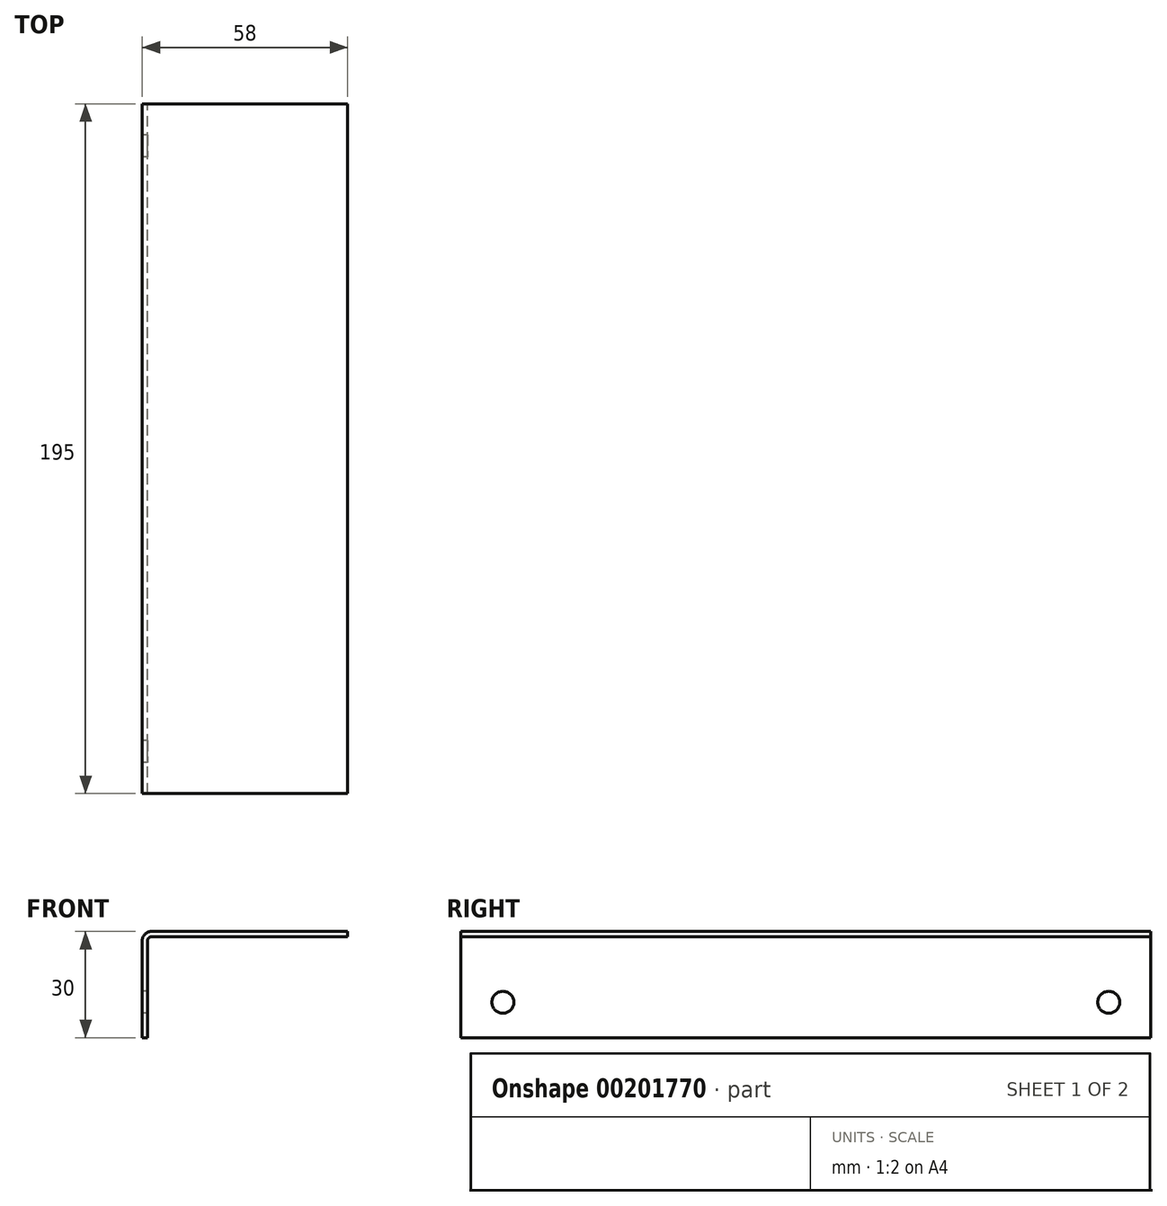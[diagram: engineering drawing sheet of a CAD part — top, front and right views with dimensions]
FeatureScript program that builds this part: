
annotation { "Feature Type Name" : "Feature", "Feature Type Description" : "" }
export const myFeature = defineFeature(function(context is Context, id is Id, definition is map)
    precondition{}
    {
        {
            var Q0;
            Q0=qCreatedBy(makeId("Front.planeOp"),FACE);
            var sketch = newSketch(context, id + "F0", { "sketchPlane" : qUnion([Q0])});
            skLineSegment(sketch, "E0", {"start": v(0, 0) * mm, "end": v(0, 30) * mm});
            skLineSegment(sketch, "E1", {"start": v(0, 30) * mm, "end": v(58, 30) * mm});
            skLineSegment(sketch, "E2.0", {"start": v(1.5, 28.5) * mm, "end": v(58, 28.5) * mm});
            skLineSegment(sketch, "E2.1", {"start": v(1.5, 0) * mm, "end": v(1.5, 28.5) * mm});
            skLineSegment(sketch, "E3", {"start": v(0, 0) * mm, "end": v(1.5, 0) * mm});
            skLineSegment(sketch, "E4", {"start": v(58, 30) * mm, "end": v(58, 28.5) * mm});
            skSolve(sketch);
        }
        {
            var Q0;
            Q0 = qSketchRegion(id + "F0", true);
            extrude(context, id + "F1", {"entities" : qUnion([Q0]), "endBound" : BoundingType.SYMMETRIC, "depth" : 195 * mm});
        }
        {
            var Q0;
            Q0=makeQuery(id+"F1.opExtrude","SWEPT_FACE",FACE,{"disambiguationData":[OSD([sQuery(id+"F0.wireOp",EDGE,"E0")])]});
            var sketch = newSketch(context, id + "F2", { "sketchPlane" : qUnion([Q0])});
            skCircle(sketch, "E5", {"center": v(-85.6, 10) * mm, "radius": 3.1 * mm});
            skCircle(sketch, "E6.MirrorC", {"center": v(85.6, 10) * mm, "radius": 3.1 * mm});
            skSolve(sketch);
        }
        {
            var Q0;
            Q0 = qSketchRegion(id + "F2", true);
            extrude(context, id + "F3", {"entities" : qUnion([Q0]), "operationType" : NewBodyOperationType.REMOVE, "oppositeDirection" : true, "depth" : 25 * mm});
        }
        {
            var Q0;
            Q0=makeQuery(id+"F1.opExtrude","SWEPT_EDGE",EDGE,{"disambiguationData":[OSD([sQuery(id+"F0.wireOp",EDGE,"E0"),sQuery(id+"F0.wireOp",EDGE,"E1")])]});
            fillet(context, id + "F4", {"entities" : qUnion([Q0]), "radius" : 2.5 * mm, "tangentPropagation" : true, "allowEdgeOverflow" : false});
        }
        {
            var Q0;
            Q0=makeQuery(id+"F1.opExtrude","SWEPT_EDGE",EDGE,{"disambiguationData":[OSD([sQuery(id+"F0.wireOp",EDGE,"E2.0"),sQuery(id+"F0.wireOp",EDGE,"E2.1")])]});
            fillet(context, id + "F5", {"entities" : qUnion([Q0]), "radius" : 1 * mm, "tangentPropagation" : true, "allowEdgeOverflow" : false});
        }
    });
